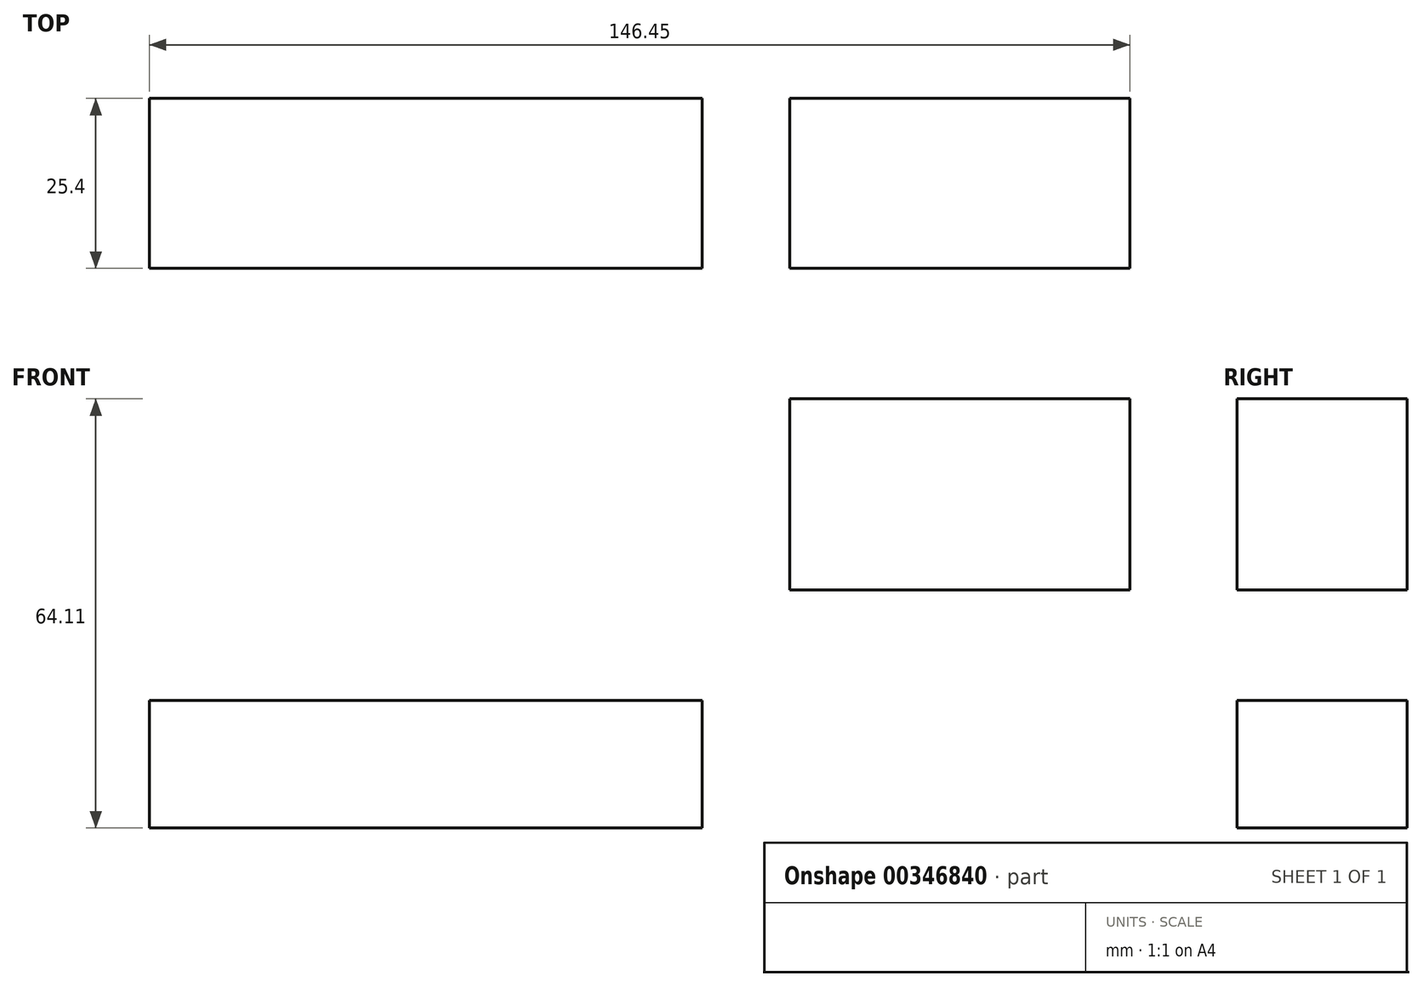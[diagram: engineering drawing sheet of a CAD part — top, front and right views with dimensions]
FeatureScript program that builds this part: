
annotation { "Feature Type Name" : "Feature", "Feature Type Description" : "" }
export const myFeature = defineFeature(function(context is Context, id is Id, definition is map)
    precondition{}
    {
        {
            var Q0;
            Q0=qCreatedBy(makeId("Front.planeOp"),FACE);
            var sketch = newSketch(context, id + "F0", { "sketchPlane" : qUnion([Q0])});
            skLineSegment(sketch, "E0.bottom", {"start": v(-41.28, 9.53) * mm, "end": v(41.27, 9.53) * mm});
            skLineSegment(sketch, "E0.top", {"start": v(-41.27, -9.52) * mm, "end": v(41.27, -9.52) * mm});
            skLineSegment(sketch, "E0.left", {"start": v(-41.28, 9.53) * mm, "end": v(-41.28, -9.52) * mm});
            skLineSegment(sketch, "E0.right", {"start": v(41.27, 9.53) * mm, "end": v(41.27, -9.52) * mm});
            skPoint(sketch, "E0.middle", {"position": v(0, 0) * mm});
            skLineSegment(sketch, "E1.bottom", {"start": v(54.38, 54.58) * mm, "end": v(105.18, 54.58) * mm});
            skLineSegment(sketch, "E1.top", {"start": v(54.38, 26) * mm, "end": v(105.18, 26) * mm});
            skLineSegment(sketch, "E1.left", {"start": v(54.38, 54.58) * mm, "end": v(54.38, 26) * mm});
            skLineSegment(sketch, "E1.right", {"start": v(105.18, 54.58) * mm, "end": v(105.18, 26) * mm});
            skPoint(sketch, "E1.middle", {"position": v(79.78, 40.3) * mm});
            skLineSegment(sketch, "E2.bottom", {"start": v(41.28, 25.44) * mm, "end": v(41.28, 25.44) * mm});
            skLineSegment(sketch, "E2.top", {"start": v(41.28, -6.4) * mm, "end": v(41.28, -6.4) * mm});
            skLineSegment(sketch, "E2.left", {"start": v(41.27, 25.44) * mm, "end": v(41.27, -6.4) * mm});
            skLineSegment(sketch, "E2.right", {"start": v(41.27, 25.44) * mm, "end": v(41.27, -6.4) * mm});
            skPoint(sketch, "E2.middle", {"position": v(41.27, 9.53) * mm});
            skArc(sketch, "E3", {"start": v(41.27, 25.44) * mm, "mid": v(44.98, 35.64) * mm, "end": v(54.38, 41.07) * mm});
            skSolve(sketch);
        }
        {
            var Q0;
            {var subQ3=sQuery(id+"F0.wireOp",EDGE,"E1.bottom");Q0=makeQuery(id+"F0.imprint","IMPRINT",FACE,{"disambiguationData":[TD([[makeQuery(id+"F0.imprint","IMPRINT",EDGE,{"derivedFrom":subQ3}),-1.0]])]});}
            var Q1;
            {var subQ1=sQuery(id+"F0.wireOp",EDGE,"E0.bottom");Q1=makeQuery(id+"F0.imprint","IMPRINT",FACE,{"disambiguationData":[TD([[makeQuery(id+"F0.imprint","IMPRINT",EDGE,{"derivedFrom":subQ1}),-1.0]])]});}
            extrude(context, id + "F1", {"entities" : qUnion([Q0, Q1]), "depth" : 25.4 * mm});
        }
    });
